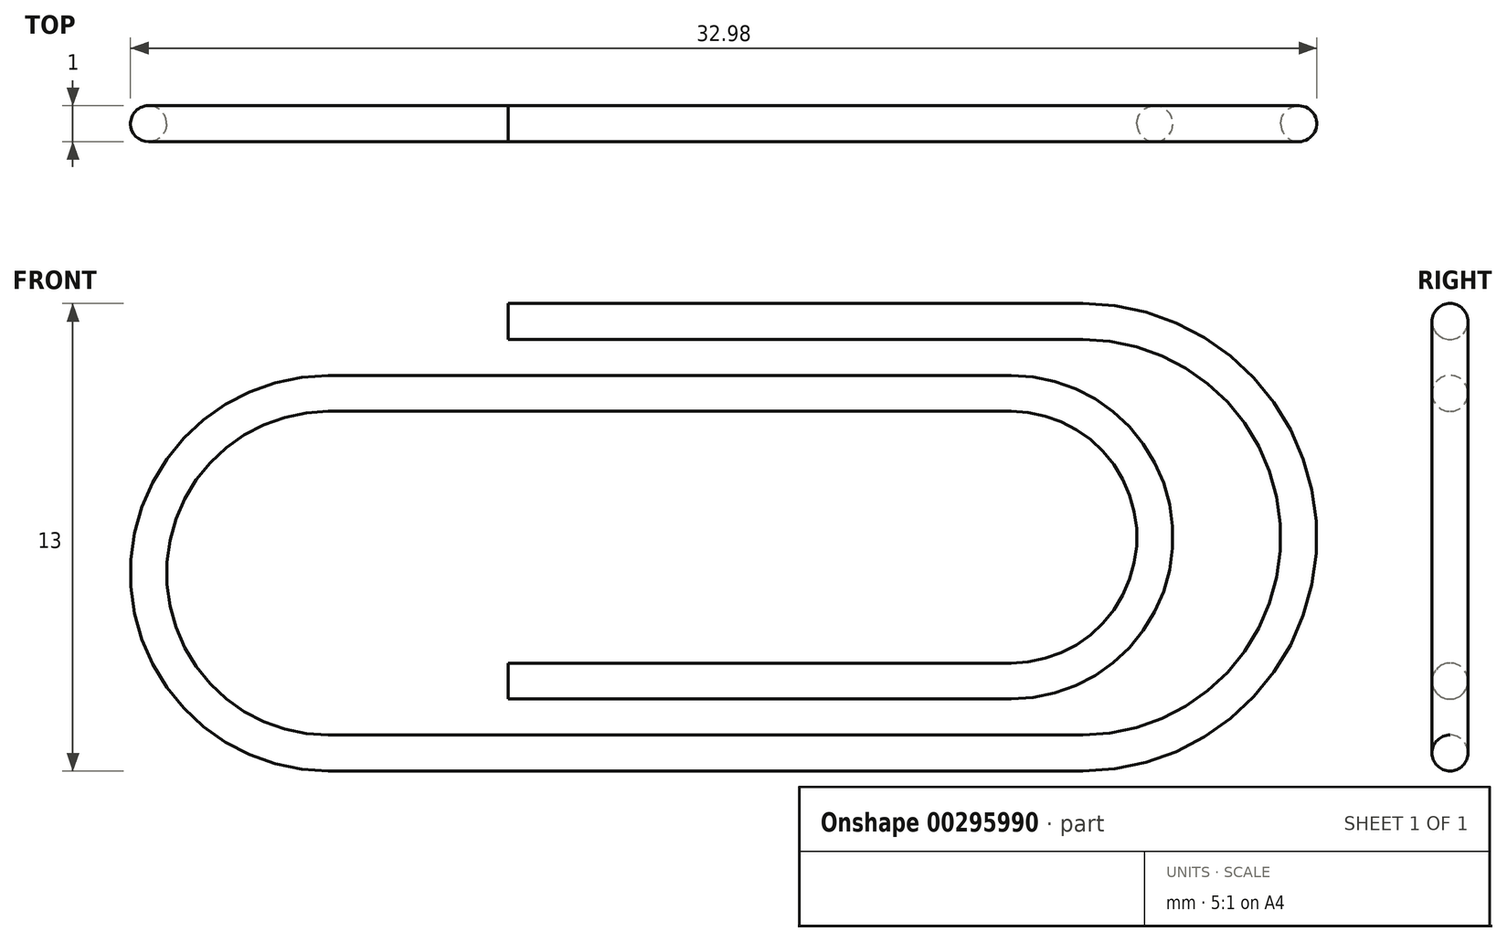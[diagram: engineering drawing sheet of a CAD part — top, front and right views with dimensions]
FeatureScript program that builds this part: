
annotation { "Feature Type Name" : "Feature", "Feature Type Description" : "" }
export const myFeature = defineFeature(function(context is Context, id is Id, definition is map)
    precondition{}
    {
        {
            var Q0;
            Q0=qCreatedBy(makeId("Front.planeOp"),FACE);
            var sketch = newSketch(context, id + "F0", { "sketchPlane" : qUnion([Q0])});
            skLineSegment(sketch, "E0", {"start": v(0, 0) * mm, "end": v(15.98, 0) * mm});
            skArc(sketch, "E1", {"start": v(15.98, 0) * mm, "mid": v(21.98, -6) * mm, "end": v(15.98, -12) * mm});
            skLineSegment(sketch, "E2", {"start": v(15.98, -12) * mm, "end": v(-5, -12) * mm});
            skArc(sketch, "E3", {"start": v(-5, -12) * mm, "mid": v(-10, -7) * mm, "end": v(-5, -2) * mm});
            skLineSegment(sketch, "E4", {"start": v(-5, -2) * mm, "end": v(13.98, -2) * mm});
            skArc(sketch, "E5", {"start": v(13.98, -2) * mm, "mid": v(17.98, -6) * mm, "end": v(13.98, -10) * mm});
            skLineSegment(sketch, "E6", {"start": v(13.98, -10) * mm, "end": v(0, -10) * mm});
            skLineSegment(sketch, "E7", {"start": v(0, 0) * mm, "end": v(0, -15.15) * mm, "construction": true});
            skSolve(sketch);
        }
        {
            var Q0;
            Q0=qCreatedBy(makeId("Right.planeOp"),FACE);
            var sketch = newSketch(context, id + "F1", { "sketchPlane" : qUnion([Q0])});
            skCircle(sketch, "E8", {"center": v(0, 0) * mm, "radius": 0.5 * mm});
            skSolve(sketch);
        }
        {
            var Q0;
            Q0=qSketchRegion(id+"F1",true);
            var Q1;
            Q1=sQuery(id+"F0.wireOp",EDGE,"E0");
            var Q2;
            Q2=sQuery(id+"F0.wireOp",EDGE,"E1");
            var Q3;
            Q3=sQuery(id+"F0.wireOp",EDGE,"E2");
            var Q4;
            Q4=sQuery(id+"F0.wireOp",EDGE,"E3");
            var Q5;
            Q5=sQuery(id+"F0.wireOp",EDGE,"E4");
            var Q6;
            Q6=sQuery(id+"F0.wireOp",EDGE,"E5");
            var Q7;
            Q7=sQuery(id+"F0.wireOp",EDGE,"E6");
            sweep(context, id + "F2", {"profiles" : qUnion([Q0]), "path" : qUnion([Q1, Q2, Q3, Q4, Q5, Q6, Q7])});
        }
    });
